# Revit family: Towel_Bar-DXV-Ashbee-D35101240_Series
name_source: partatom
category: Specialty Equipment
revit_build: Autodesk Revit 2014 (Build: 20130308_1515(x64)
units: mm (PartAtom-declared; Revit-internal decimal feet)

## types (3) — shared parameters
Assembly Code = C1030200
Default Elevation = 40"
Description = Ashbee 24" Towel Bar
Height = 2 3/8"
Installation Type = Surface Mounted
Length = 3 1/8"
Manufacturer = DXV
Price = Prices may vary. Please consult Manufacturer Representative for most up-to-date price list.
Product Documentation Link = http://dxv01.blob.core.windows.net
Product Page URL = http://www.dxv.com
Revised Date = 01/25/2017
URL = http://www.dxv.com
Warranty Documentation Link = https://www.dxv.com
Width = 23 5/8"

## per-type parameters (varying)
| type | Finish | Material |
| D35101240.100 | Brass-DXV-100-Polished Chrome | Brass-DXV-100-Polished Chrome |
| D35101240.144 | Brass-DXV-144-Brushed Nickel | Brass-DXV-144-Brushed Nickel |
| D35101240.150 | Brass-DXV-150-Platinum Nickel | Brass-DXV-150-Platinum Nickel |

note: column(s) folded — value = type name in every type: Model

## geometry (parser evidence)
native form markers: Sweep x2
no freeform markers — native parametric forms only
